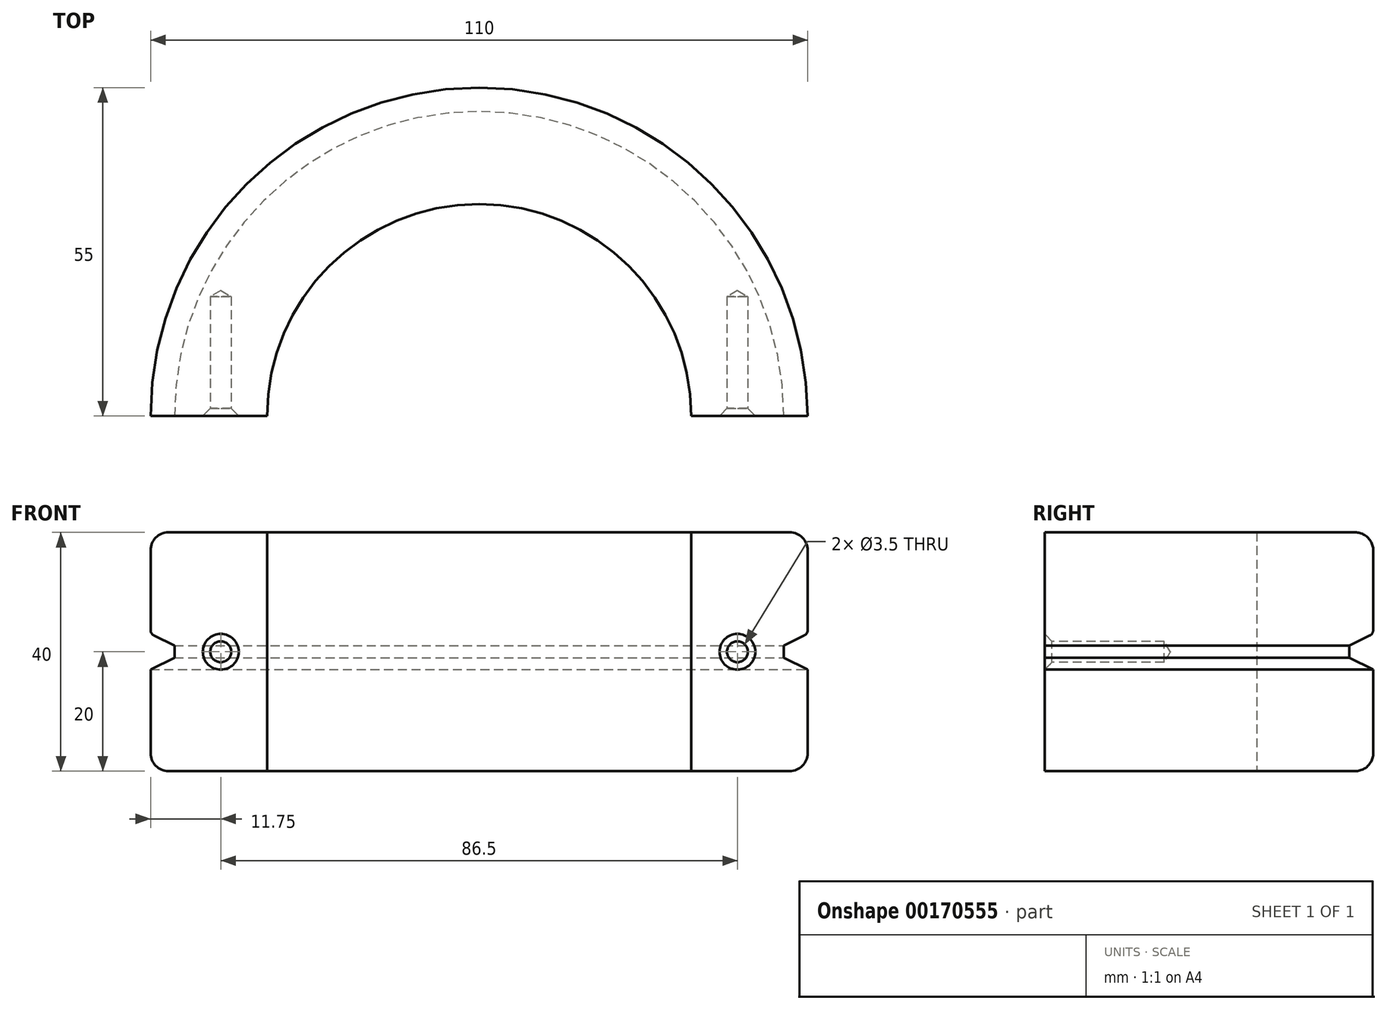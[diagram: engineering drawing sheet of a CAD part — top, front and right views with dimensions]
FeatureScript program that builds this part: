
annotation { "Feature Type Name" : "Feature", "Feature Type Description" : "" }
export const myFeature = defineFeature(function(context is Context, id is Id, definition is map)
    precondition{}
    {
        {
            var Q0;
            Q0=qCreatedBy(makeId("Top.planeOp"),FACE);
            var sketch = newSketch(context, id + "F0", { "sketchPlane" : qUnion([Q0])});
            skCircle(sketch, "E0", {"center": v(0, 0) * mm, "radius": 35.5 * mm});
            skCircle(sketch, "E1", {"center": v(0, 0) * mm, "radius": 55 * mm});
            skLineSegment(sketch, "E2", {"start": v(-55, 0) * mm, "end": v(-35.5, 0) * mm});
            skLineSegment(sketch, "E3", {"start": v(35.5, 0) * mm, "end": v(55, 0) * mm});
            skSolve(sketch);
        }
        {
            var Q0;
            {var subQ0=sQuery(id+"F0.wireOp",EDGE,"E2");Q0=makeQuery(id+"F0.imprint","IMPRINT",FACE,{"disambiguationData":[TD([[makeQuery(id+"F0.imprint","IMPRINT",EDGE,{"derivedFrom":subQ0}),1.0]])]});}
            extrude(context, id + "F1", {"entities" : qUnion([Q0]), "depth" : 40 * mm});
        }
        {
            var Q0;
            Q0=makeQuery(id+"F1.opExtrude","SWEPT_FACE",FACE,{"disambiguationData":[OSD([sQuery(id+"F0.wireOp",EDGE,"E3")])]});
            var sketch = newSketch(context, id + "F2", { "sketchPlane" : qUnion([Q0])});
            skLineSegment(sketch, "E4", {"start": v(55, 17) * mm, "end": v(51, 19) * mm});
            skLineSegment(sketch, "E5", {"start": v(51, 19) * mm, "end": v(51, 21) * mm});
            skLineSegment(sketch, "E6", {"start": v(51, 21) * mm, "end": v(55, 23) * mm});
            skLineSegment(sketch, "E7", {"start": v(55, 20) * mm, "end": v(51, 20) * mm});
            skLineSegment(sketch, "E8", {"start": v(51, 20) * mm, "end": v(55, 20) * mm, "construction": true});
            skSolve(sketch);
        }
        {
            var Q0;
            {var subQ0=sQuery(id+"F2.wireOp",EDGE,"E6");Q0=makeQuery(id+"F2.imprint","IMPRINT",FACE,{"disambiguationData":[TD([[makeQuery(id+"F2.imprint","IMPRINT",EDGE,{"derivedFrom":subQ0}),-1.0]])]});}
            var Q1;
            {var subQ0=sQuery(id+"F2.wireOp",EDGE,"E4");Q1=makeQuery(id+"F2.imprint","IMPRINT",FACE,{"disambiguationData":[TD([[makeQuery(id+"F2.imprint","IMPRINT",EDGE,{"derivedFrom":subQ0}),-1.0]])]});}
            var Q2;
            Q2=makeQuery(id+"F1.opExtrude","SWEPT_FACE",FACE,{"disambiguationData":[OSD([sQuery(id+"F0.wireOp",EDGE,"E1")])]});
            revolve(context, id + "F3", {"operationType" : NewBodyOperationType.REMOVE, "entities" : qUnion([Q0, Q1]), "axis" : qUnion([Q2]), "revolveType" : RevolveType.FULL, "oppositeDirection" : true});
        }
        {
            var Q0;
            Q0=makeQuery(id+"F1.opExtrude","SWEPT_FACE",FACE,{"disambiguationData":[OSD([sQuery(id+"F0.wireOp",EDGE,"E3")])]});
            var sketch = newSketch(context, id + "F4", { "sketchPlane" : qUnion([Q0])});
            skLineSegment(sketch, "E9", {"start": v(35.5, 20) * mm, "end": v(51, 20) * mm});
            skPoint(sketch, "E10", {"position": v(43.25, 20) * mm});
            skSolve(sketch);
        }
        {
            var Q0;
            Q0=sQuery(id+"F4.wireOp",VERTEX,"E10");
            var Q1;
            Q1=makeQuery(id+"F1.opExtrude","SWEPT_BODY",BODY,{"disambiguationData":[OSD([sQuery(id+"F0.wireOp",EDGE,"E0"),sQuery(id+"F0.wireOp",EDGE,"E1"),sQuery(id+"F0.wireOp",EDGE,"E2"),sQuery(id+"F0.wireOp",EDGE,"E3")])]});
            hole(context, id + "F5", {"style" : HoleStyle.C_SINK, "endStyle" : HoleEndStyle.BLIND, "holeDiameter" : 3.5 * mm, "cSinkDiameter" : 6 * mm, "cSinkAngle" : 90 * degree, "holeDepth" : 20 * mm, "locations" : qUnion([Q0]), "scope" : qUnion([Q1])});
        }
        {
            var Q0;
            Q0=makeQuery(id+"F1.opExtrude","SWEPT_FACE",FACE,{"disambiguationData":[OSD([sQuery(id+"F0.wireOp",EDGE,"E2")])]});
            var sketch = newSketch(context, id + "F6", { "sketchPlane" : qUnion([Q0])});
            skLineSegment(sketch, "E11", {"start": v(-51, 20) * mm, "end": v(-35.5, 20) * mm});
            skPoint(sketch, "E12", {"position": v(-43.25, 20) * mm});
            skSolve(sketch);
        }
        {
            var Q0;
            Q0=sQuery(id+"F6.wireOp",VERTEX,"E12");
            var Q1;
            Q1=makeQuery(id+"F1.opExtrude","SWEPT_BODY",BODY,{"disambiguationData":[OSD([sQuery(id+"F0.wireOp",EDGE,"E0"),sQuery(id+"F0.wireOp",EDGE,"E1"),sQuery(id+"F0.wireOp",EDGE,"E2"),sQuery(id+"F0.wireOp",EDGE,"E3")])]});
            hole(context, id + "F7", {"style" : HoleStyle.C_SINK, "endStyle" : HoleEndStyle.BLIND, "holeDiameter" : 3.5 * mm, "cSinkDiameter" : 6 * mm, "cSinkAngle" : 90 * degree, "holeDepth" : 20 * mm, "locations" : qUnion([Q0]), "scope" : qUnion([Q1])});
        }
        {
            var Q0;
            Q0=makeQuery(id+"F1.opExtrude","CAP_EDGE",EDGE,{"disambiguationData":[OSD([sQuery(id+"F0.wireOp",EDGE,"E1")])],"isStart":true});
            var Q1;
            Q1=makeQuery(id+"F1.opExtrude","CAP_EDGE",EDGE,{"disambiguationData":[OSD([sQuery(id+"F0.wireOp",EDGE,"E1")])],"isStart":false});
            fillet(context, id + "F8", {"entities" : qUnion([Q0, Q1]), "radius" : 3 * mm, "tangentPropagation" : true, "allowEdgeOverflow" : false});
        }
        {
            var Q0;
            Q0=makeQuery(id+"F3.boolean.opBoolean","COPY",EDGE,{"derivedFrom":makeQuery(id+"F3.opRevolve","SWEPT_EDGE",EDGE,{"disambiguationData":[OSD([sQuery(id+"F0.wireOp",EDGE,"E1"),sQuery(id+"F0.wireOp",EDGE,"E3"),sQuery(id+"F2.wireOp",EDGE,"E6")])]})});
            var Q1;
            Q1=makeQuery(id+"F3.boolean.opBoolean","COPY",EDGE,{"derivedFrom":makeQuery(id+"F3.opRevolve","SWEPT_EDGE",EDGE,{"disambiguationData":[OSD([sQuery(id+"F0.wireOp",EDGE,"E1"),sQuery(id+"F0.wireOp",EDGE,"E3"),sQuery(id+"F2.wireOp",EDGE,"E4")])]})});
            fillet(context, id + "F9", {"entities" : qUnion([Q0, Q1]), "radius" : 1 * mm, "tangentPropagation" : true, "allowEdgeOverflow" : false});
        }
    });
